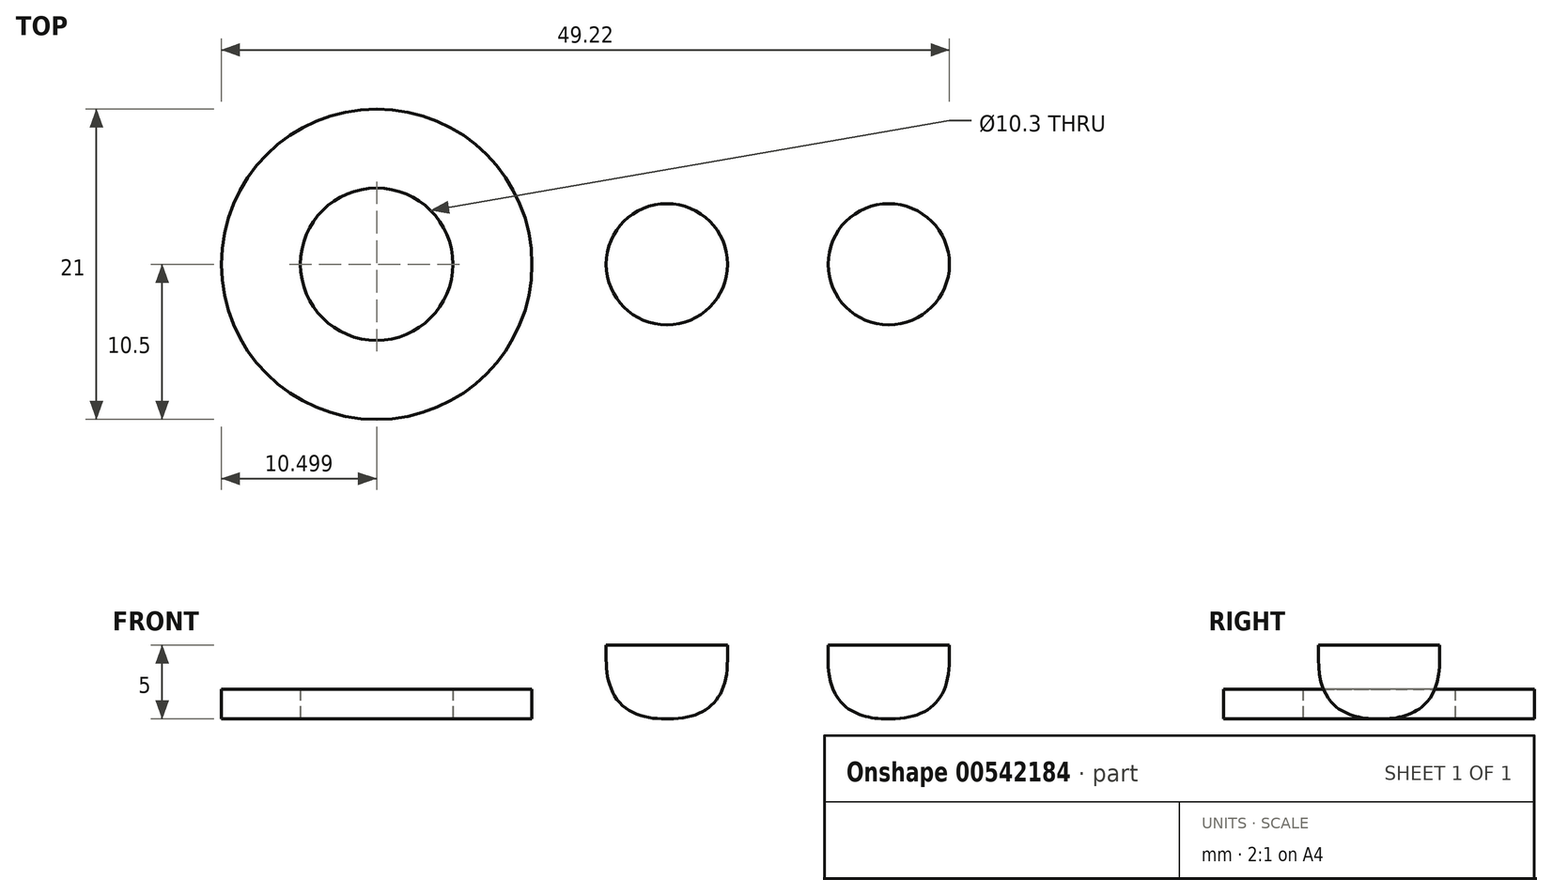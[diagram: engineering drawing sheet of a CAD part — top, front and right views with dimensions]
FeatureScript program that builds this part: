
annotation { "Feature Type Name" : "Feature", "Feature Type Description" : "" }
export const myFeature = defineFeature(function(context is Context, id is Id, definition is map)
    precondition{}
    {
        {
            var Q0;
            Q0=qCreatedBy(makeId("Top.planeOp"),FACE);
            var sketch = newSketch(context, id + "F0", { "sketchPlane" : qUnion([Q0])});
            skCircle(sketch, "E0", {"center": v(0, 0) * mm, "radius": 4.1 * mm});
            skCircle(sketch, "E1", {"center": v(-19.62, 0) * mm, "radius": 10.5 * mm});
            skCircle(sketch, "E2", {"center": v(-19.62, 0) * mm, "radius": 5.15 * mm});
            skSolve(sketch);
        }
        {
            var Q0;
            Q0=makeQuery(id+"F0.imprint","IMPRINT",FACE,{"disambiguationData":[TD([[makeQuery(id+"F0.imprint","IMPRINT",EDGE,{"derivedFrom":sQuery(id+"F0.wireOp",EDGE,"E0")}),1.0]])]});
            extrude(context, id + "F1", {"entities" : qUnion([Q0]), "depth" : 5 * mm, "offsetDistance" : 25 * mm});
        }
        {
            var Q0;
            Q0=makeQuery(id+"F1.opExtrude","SWEPT_BODY",BODY,{"disambiguationData":[OSD([sQuery(id+"F0.wireOp",EDGE,"E0")])]});
            transform(context, id + "F2", {"entities" : qUnion([Q0]), "transformType" : TransformType.TRANSLATION_3D, "dx" : 15 * mm, "dy" : 0 * mm, "dz" : 0 * mm, "makeCopy" : true});
        }
        {
            var Q0;
            Q0=makeQuery(id+"F1.opExtrude","CAP_EDGE",EDGE,{"disambiguationData":[OSD([sQuery(id+"F0.wireOp",EDGE,"E0")])],"isStart":true});
            var Q1;
            Q1=makeQuery(id+"F2.opPattern","COPY",EDGE,{"derivedFrom":makeQuery(id+"F1.opExtrude","CAP_EDGE",EDGE,{"disambiguationData":[OSD([sQuery(id+"F0.wireOp",EDGE,"E0")])],"isStart":true}),"instanceName":"1"});
            fillet(context, id + "F3", {"entities" : qUnion([Q0, Q1]), "radius" : 4 * mm, "tangentPropagation" : true, "rho" : 0.5, "crossSection" : FilletCrossSection.CONIC, "allowEdgeOverflow" : false});
        }
        {
            var Q0;
            Q0=makeQuery(id+"F0.imprint","IMPRINT",FACE,{"disambiguationData":[TD([[makeQuery(id+"F0.imprint","IMPRINT",EDGE,{"derivedFrom":sQuery(id+"F0.wireOp",EDGE,"E1")}),1.0]])]});
            extrude(context, id + "F4", {"entities" : qUnion([Q0]), "depth" : 2 * mm, "offsetDistance" : 25 * mm});
        }
    });
